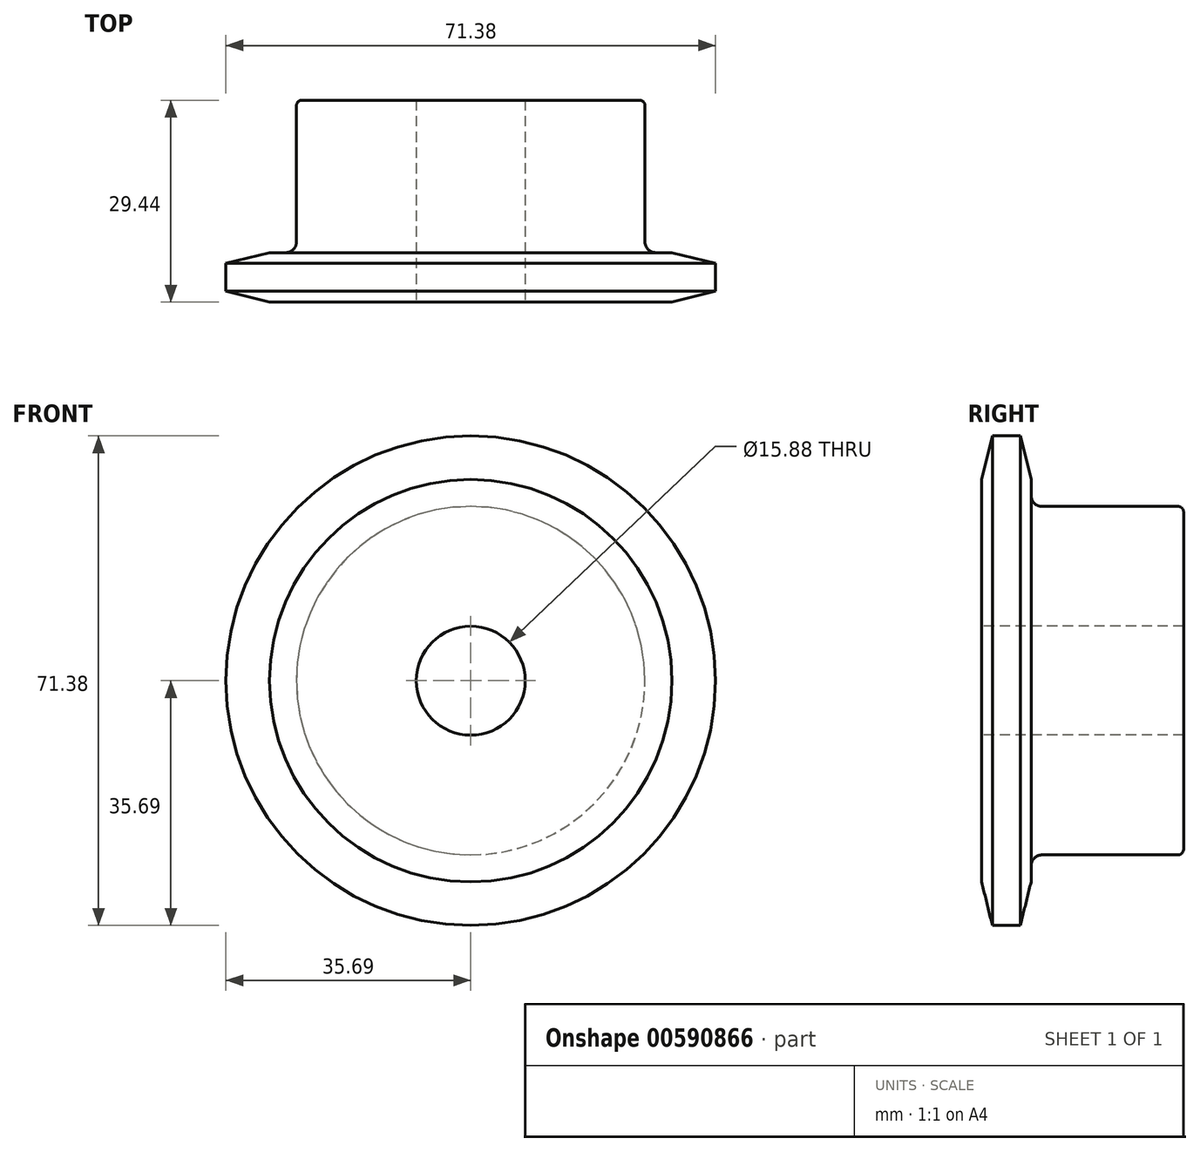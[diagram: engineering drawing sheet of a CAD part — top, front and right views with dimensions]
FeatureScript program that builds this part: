
annotation { "Feature Type Name" : "Feature", "Feature Type Description" : "" }
export const myFeature = defineFeature(function(context is Context, id is Id, definition is map)
    precondition{}
    {
        {
            var Q0;
            Q0=qCreatedBy(makeId("Right.planeOp"),FACE);
            var sketch = newSketch(context, id + "F0", { "sketchPlane" : qUnion([Q0])});
            skLineSegment(sketch, "E0", {"start": v(0, 0) * mm, "end": v(31.8, 0) * mm, "construction": true});
            skLineSegment(sketch, "E1.bottom", {"start": v(0, 8.18) * mm, "end": v(7.21, 8.18) * mm});
            skLineSegment(sketch, "E1.top", {"start": v(0, 35.69) * mm, "end": v(7.21, 35.69) * mm});
            skLineSegment(sketch, "E1.left", {"start": v(0, 8.18) * mm, "end": v(0, 35.69) * mm});
            skLineSegment(sketch, "E1.right", {"start": v(7.21, 8.18) * mm, "end": v(7.21, 35.69) * mm});
            skLineSegment(sketch, "E2.bottom", {"start": v(0, 25.4) * mm, "end": v(29.44, 25.4) * mm});
            skLineSegment(sketch, "E2.top", {"start": v(0, 7.94) * mm, "end": v(29.44, 7.94) * mm});
            skLineSegment(sketch, "E2.left", {"start": v(0, 25.4) * mm, "end": v(0, 7.94) * mm});
            skLineSegment(sketch, "E2.right", {"start": v(29.44, 25.4) * mm, "end": v(29.44, 7.94) * mm});
            skLineSegment(sketch, "E3.MirrorCS", {"start": v(0, -7.94) * mm, "end": v(29.44, -7.94) * mm});
            skLineSegment(sketch, "E4.MirrorCS", {"start": v(29.44, -25.4) * mm, "end": v(29.44, -7.94) * mm});
            skLineSegment(sketch, "E5.MirrorCS", {"start": v(0, -8.18) * mm, "end": v(0, -35.69) * mm});
            skLineSegment(sketch, "E6.MirrorCS", {"start": v(0, -25.4) * mm, "end": v(0, -7.94) * mm});
            skLineSegment(sketch, "E7.MirrorCS", {"start": v(7.21, -8.18) * mm, "end": v(7.21, -35.69) * mm});
            skLineSegment(sketch, "E8.MirrorCS", {"start": v(0, -25.4) * mm, "end": v(29.44, -25.4) * mm});
            skLineSegment(sketch, "E9.MirrorCS", {"start": v(0, -8.18) * mm, "end": v(7.21, -8.18) * mm});
            skLineSegment(sketch, "E10.MirrorCS", {"start": v(0, -35.69) * mm, "end": v(7.21, -35.69) * mm});
            skSolve(sketch);
        }
        {
            var Q0;
            {var subQ0=sQuery(id+"F0.wireOp",EDGE,"E1.top");Q0=makeQuery(id+"F0.imprint","IMPRINT",FACE,{"disambiguationData":[TD([[makeQuery(id+"F0.imprint","IMPRINT",EDGE,{"derivedFrom":subQ0}),-1.0]])]});}
            var Q1;
            {var subQ0=sQuery(id+"F0.wireOp",EDGE,"E1.bottom");Q1=makeQuery(id+"F0.imprint","IMPRINT",FACE,{"disambiguationData":[TD([[makeQuery(id+"F0.imprint","IMPRINT",EDGE,{"derivedFrom":subQ0}),1.0]])]});}
            var Q2;
            {var subQ5=sQuery(id+"F0.wireOp",EDGE,"E1.bottom");Q2=makeQuery(id+"F0.imprint","IMPRINT",FACE,{"disambiguationData":[TD([[makeQuery(id+"F0.imprint","IMPRINT",EDGE,{"derivedFrom":subQ5}),-1.0]])]});}
            var Q3;
            Q3=sQuery(id+"F0.wireOp",EDGE,"E0");
            revolve(context, id + "F1", {"entities" : qUnion([Q0, Q1, Q2]), "axis" : qUnion([Q3]), "revolveType" : RevolveType.FULL});
        }
        {
            var Q0;
            Q0=makeQuery(id+"F1.opRevolve","SWEPT_EDGE",EDGE,{"disambiguationData":[OSD([sQuery(id+"F0.wireOp",EDGE,"E1.right"),sQuery(id+"F0.wireOp",EDGE,"E2.bottom")])]});
            fillet(context, id + "F2", {"entities" : qUnion([Q0]), "radius" : 1.59 * mm, "tangentPropagation" : true, "allowEdgeOverflow" : false});
        }
        {
            var Q0;
            Q0=makeQuery(id+"F1.opRevolve","SWEPT_EDGE",EDGE,{"disambiguationData":[OSD([sQuery(id+"F0.wireOp",EDGE,"E2.bottom"),sQuery(id+"F0.wireOp",EDGE,"E2.right")])]});
            fillet(context, id + "F3", {"entities" : qUnion([Q0]), "radius" : 0.8 * mm, "tangentPropagation" : true, "allowEdgeOverflow" : false});
        }
        {
            var Q0;
            Q0=makeQuery(id+"F1.opRevolve","SWEPT_EDGE",EDGE,{"disambiguationData":[OSD([sQuery(id+"F0.wireOp",EDGE,"E1.top"),sQuery(id+"F0.wireOp",EDGE,"E1.left")])]});
            var Q1;
            Q1=makeQuery(id+"F1.opRevolve","SWEPT_EDGE",EDGE,{"disambiguationData":[OSD([sQuery(id+"F0.wireOp",EDGE,"E1.top"),sQuery(id+"F0.wireOp",EDGE,"E1.right")])]});
            chamfer(context, id + "F4", {"entities" : qUnion([Q0, Q1]), "chamferType" : ChamferType.TWO_OFFSETS, "width1" : 6.35 * mm, "oppositeDirection" : false, "width2" : 1.57 * mm, "tangentPropagation" : true});
        }
    });
